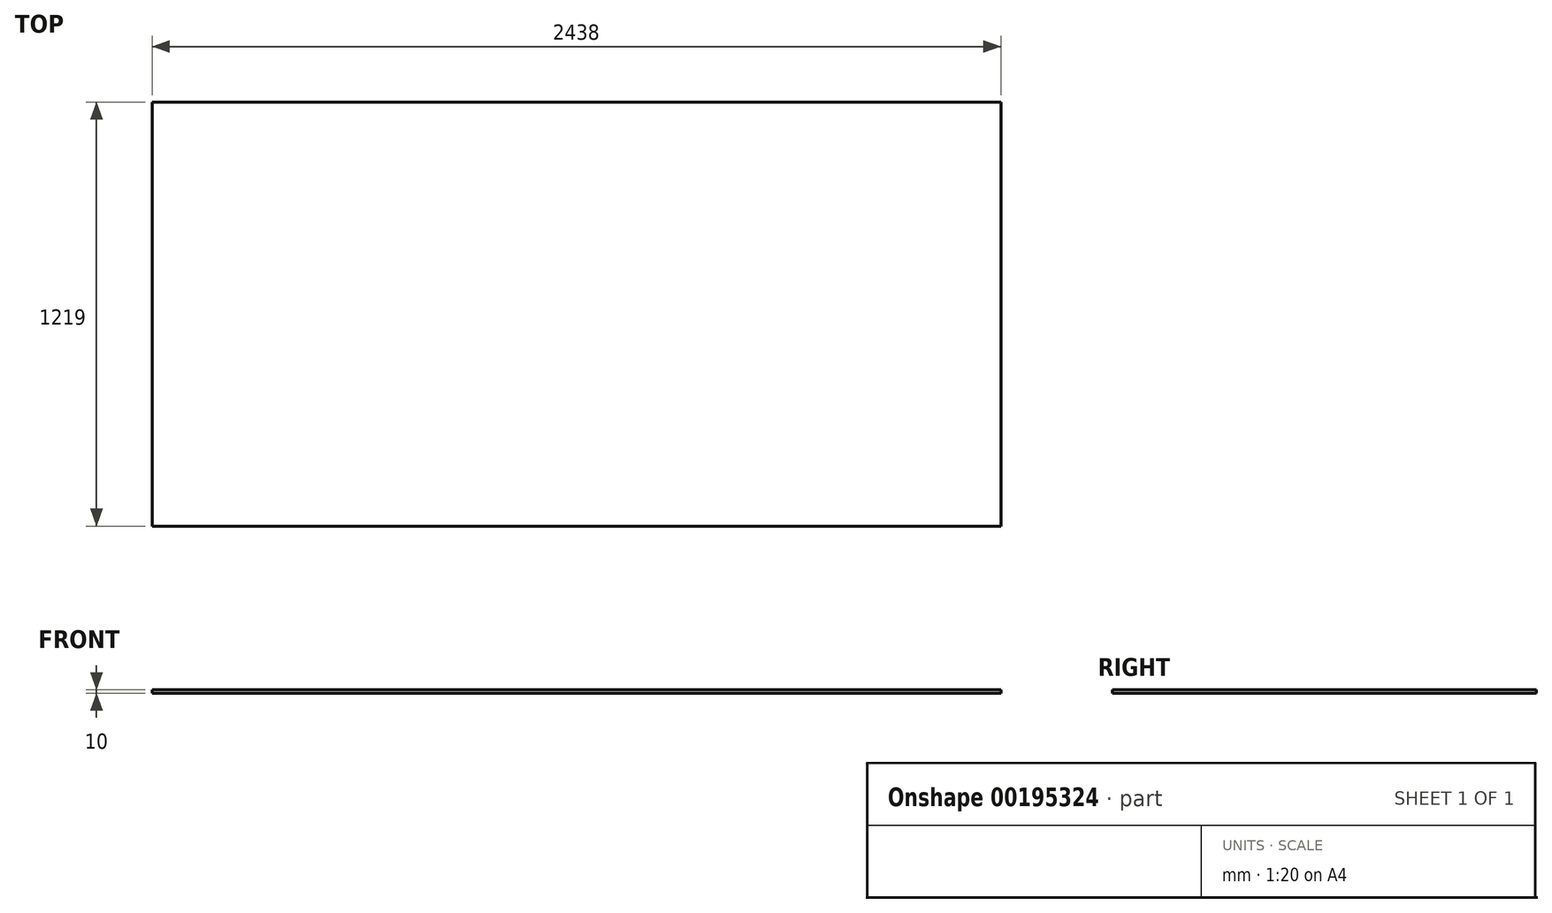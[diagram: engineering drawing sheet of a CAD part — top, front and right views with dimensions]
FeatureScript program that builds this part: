
annotation { "Feature Type Name" : "Feature", "Feature Type Description" : "" }
export const myFeature = defineFeature(function(context is Context, id is Id, definition is map)
    precondition{}
    {
        {
            var Q0;
            Q0=qCreatedBy(makeId("Top.planeOp"),FACE);
            var sketch = newSketch(context, id + "F0", { "sketchPlane" : qUnion([Q0])});
            skLineSegment(sketch, "E0.bottom", {"start": v(0, 0) * mm, "end": v(2438, 0) * mm});
            skLineSegment(sketch, "E0.top", {"start": v(0, -1219) * mm, "end": v(2438, -1219) * mm});
            skLineSegment(sketch, "E0.left", {"start": v(0, 0) * mm, "end": v(0, -1219) * mm});
            skLineSegment(sketch, "E0.right", {"start": v(2438, 0) * mm, "end": v(2438, -1219) * mm});
            skSolve(sketch);
        }
        {
            var Q0;
            Q0=makeQuery(id+"F0.imprint","IMPRINT",FACE,{"disambiguationData":[TD([[makeQuery(id+"F0.imprint","IMPRINT",EDGE,{"derivedFrom":sQuery(id+"F0.wireOp",EDGE,"E0.bottom")}),-1.0]])]});
            extrude(context, id + "F1", {"entities" : qUnion([Q0]), "depth" : 10 * mm});
        }
    });
